# Revit family: Basketball-Structure_Wall-Mount_Side-Fold_PKGxxSFRG
name_source: partatom
category: Generic Models
units: mm (PartAtom-declared; Revit-internal decimal feet)

## family parameters
Always vertical = Yes
Can host rebar = No
Cut with Voids When Loaded = No
Maintain Annotation Orientation = No
OmniClass Number = 23.40.50.34.24
OmniClass Title = Nets
Part Type = Normal
Room Calculation Point = No
Round Connector Dimension = Use Diameter
Shared = No
Work Plane-Based = No

## types (3) — shared parameters
Backboard Frame Material = Steel - Tubular Support
Backboard Height = 3' - 6"
Backboard Material = Fiberglass - Backboard
Building Codes = https://www.brpbybison.com
Construction Details = https://www.arcat.com
Default Elevation = 0' - 0"
Description = IPI by Bison Gymnasium Equipment
Green Building-LEED = https://www.arcat.com
Hoop Finish = Powder Coat - Playground Orange
Installation-Fabrication = http://www.ipibybison.com
Keynote = 11 66 00
Manufacturer = IPI by Bison
Manufacturer Fax = 888-438-5312
Manufacturer Website = http://www.ipibybison.com
Model = As Specified
Netting = Finish - IPI by Bison - White Netting
PKG46STRG Extension Range = 48" to 72"
PKG68STRG Extension Range = 72" to 96"
PKG82STRG Extension Range = 96" to 144"
Product Data = http://www.arcat.com
Revision = R1_2018-09
Sales Information = http://www.ipibybison.com
Specification = https://www.arcat.com
Support Tubing Diameter = 0' - 1 29/32"
Support Tubing Material = Steel - Tubular Support
Suspension Type = Telescoping
Test Data = http://www.ipibybison.com
URL = https://ipibybison.com
Wall Plate Material = Wood
Width = 6' - 0"

## per-type parameters (varying)
| type | Extension Depth |
| PKG46STRG | 4' - 0" |
| PKG68STRG | 6' - 0" |
| PKG82STRG | 8' - 0" |

## geometry (parser evidence)
native form markers: Blend x4, Sweep x6
no freeform markers — native parametric forms only
